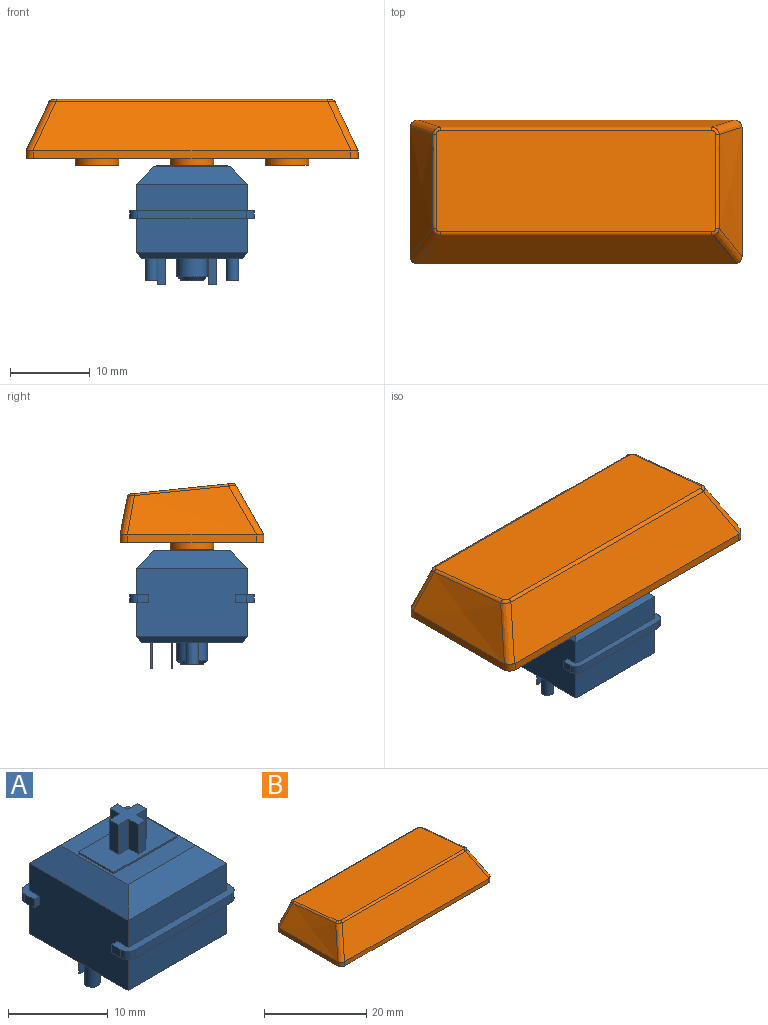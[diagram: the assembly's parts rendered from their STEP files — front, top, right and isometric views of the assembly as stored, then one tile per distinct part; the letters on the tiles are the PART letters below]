
ASSEMBLY  parts=2 mates=1
PART A: 69 faces, bbox 15.6x15.6x18.6 mm
  f0: plane 15.6x2.3mm, normal (0,0,-1), area 14.4mm2, adj f2,f3,f28,f30,f35,f60,f62,f63
  f1: plane 15.6x2.3mm, normal (0,0,-1), area 14.4mm2, adj f28,f30,f33,f34,f36,f59,f61,f64
  f2: plane 1.3x1mm, normal (1,0,0), area 1.3mm2, adj f0,f32,f62,f66
  f3: plane 1.3x1mm, normal (-1,0,0), area 1.3mm2, adj f0,f32,f63,f68
  f4: plane 15.6x2.3mm, normal (0,0,1), area 14.4mm2, adj f28,f30,f31,f33,f34,f36,f61,f64
  f5: plane 14x2.2mm, normal (-0.71,0,0.71), area 36.7mm2, adj f6,f7,f26,f30
  f6: plane 14x2.2mm, normal (0,-0.71,0.71), area 36.7mm2, adj f5,f7,f27,f31
  f7: plane 9.6x9.6mm, normal (0,0,1), area 47.2mm2, adj f5,f6,f8,f9,f10,f11,f26,f27
  f8: plane 5x0.2mm, normal (1,0,0), area 1mm2, adj f7,f9,f11,f12
  f9: plane 9x0.2mm, normal (0,1,0), area 1.8mm2, adj f7,f8,f10,f12
  f10: plane 5x0.2mm, normal (-1,0,0), area 1mm2, adj f7,f9,f11,f12
  f11: plane 9x0.2mm, normal (0,-1,0), area 1.8mm2, adj f7,f8,f10,f12
  f12: plane 9x5mm, normal (0,0,1), area 36.9mm2, adj f8,f9,f10,f11,f13,f14,f15,f16
  f13: plane 3.6x1.35mm, normal (1,0,0), area 4.9mm2, adj f12,f14,f24,f25
  f14: plane 3.6x1.08mm, normal (0,1,0), area 3.9mm2, adj f12,f13,f15,f25
  f15: plane 3.6x1.35mm, normal (-1,0,0), area 4.9mm2, adj f12,f14,f16,f25
  f16: plane 3.6x1.46mm, normal (0,1,0), area 5.3mm2, adj f12,f15,f17,f25
  f17: plane 3.6x1.3mm, normal (-1,0,0), area 4.7mm2, adj f12,f16,f18,f25
  f18: plane 3.6x1.46mm, normal (0,-1,0), area 5.3mm2, adj f12,f17,f19,f25
  f19: plane 3.6x1.35mm, normal (-1,0,0), area 4.9mm2, adj f12,f18,f20,f25
  f20: plane 3.6x1.08mm, normal (0,-1,0), area 3.9mm2, adj f12,f19,f21,f25
  f21: plane 3.6x1.35mm, normal (1,0,0), area 4.9mm2, adj f12,f20,f22,f25
  f22: plane 3.6x1.46mm, normal (0,-1,0), area 5.3mm2, adj f12,f21,f23,f25
  f23: plane 3.6x1.3mm, normal (1,0,0), area 4.7mm2, adj f12,f22,f24,f25
  f24: plane 3.6x1.46mm, normal (0,1,0), area 5.3mm2, adj f12,f13,f23,f25
  f25: plane 4x4mm, normal (0,0,1), area 8.1mm2, adj f13,f14,f15,f16,f17,f18,f19,f20
  f26: plane 14x2.2mm, normal (0,0.71,0.71), area 36.7mm2, adj f5,f7,f27,f29
  f27: plane 14x2.2mm, normal (0.71,0,0.71), area 36.7mm2, adj f6,f7,f26,f28
  f28: plane 14x8.6mm, normal (1,0,0), area 117.4mm2, adj f0,f1,f4,f27,f29,f31,f32,f55
  f29: plane 14x3.3mm, normal (0,1,0), area 46.2mm2, adj f26,f28,f30,f32
  f30: plane 14x8.6mm, normal (-1,0,0), area 117.4mm2, adj f0,f1,f4,f5,f29,f31,f32,f57
  f31: plane 14x3.3mm, normal (0,-1,0), area 46.2mm2, adj f4,f6,f28,f30
  f32: plane 15.6x2.3mm, normal (0,0,1), area 14.4mm2, adj f2,f3,f28,f29,f30,f35,f62,f63
  f33: plane 13.6x1mm, normal (0,-1,0), area 13.6mm2, adj f1,f4,f61,f64
  f34: plane 1.3x1mm, normal (1,0,0), area 1.3mm2, adj f1,f4,f61,f65
  f35: plane 13.6x1mm, normal (0,1,0), area 13.6mm2, adj f0,f32,f62,f63
  f36: plane 1.3x1mm, normal (-1,0,0), area 1.3mm2, adj f1,f4,f64,f67
  f37: plane 2.85x2.85mm, normal (0,0,-1), area 6.4mm2, adj f38
  f38: cone r=1.43mm half-angle=45deg, axis (0,0,1), area 7.4mm2, adj f37,f43
  f39: plane 1x0.2mm, normal (0,0,-1), area 0.2mm2, adj f44,f45,f46,f47
  f40: plane 1x0.2mm, normal (0,0,-1), area 0.2mm2, adj f48,f49,f50,f51
  f41: plane 1.6x1.6mm, normal (0,0,-1), area 2mm2, adj f52
  f42: plane 1.6x1.6mm, normal (0,0,-1), area 2mm2, adj f53
  f43: cylinder r=1.93mm len=3.85mm, axis (0,0,1), area 27.8mm2, adj f38,f54
  f44: plane 3.3x0.2mm, normal (-1,0,0), area 0.7mm2, adj f39,f45,f47,f54
  f45: plane 3.3x1mm, normal (0,1,0), area 3.3mm2, adj f39,f44,f46,f54
  f46: plane 3.3x0.2mm, normal (1,0,0), area 0.7mm2, adj f39,f45,f47,f54
  f47: plane 3.3x1mm, normal (0,-1,0), area 3.3mm2, adj f39,f44,f46,f54
  f48: plane 3.3x0.2mm, normal (-1,0,0), area 0.7mm2, adj f40,f49,f51,f54
  f49: plane 3.3x1mm, normal (0,1,0), area 3.3mm2, adj f40,f48,f50,f54
  f50: plane 3.3x0.2mm, normal (1,0,0), area 0.7mm2, adj f40,f49,f51,f54
  f51: plane 3.3x1mm, normal (0,-1,0), area 3.3mm2, adj f40,f48,f50,f54
  f52: cylinder r=0.8mm len=2.8mm, axis (0,0,1), area 14.1mm2, adj f41,f54
  f53: cylinder r=0.8mm len=2.8mm, axis (0,0,1), area 14.1mm2, adj f42,f54
  f54: plane 12.6x12.6mm, normal (0,0,-1), area 142.7mm2, adj f43,f44,f45,f46,f47,f48,f49,f50
  f55: plane 14x0.7mm, normal (0.71,0,-0.71), area 13.2mm2, adj f28,f54,f56,f58
  f56: plane 14x0.7mm, normal (0,0.71,-0.71), area 13.2mm2, adj f54,f55,f57,f60
  f57: plane 14x0.7mm, normal (-0.71,0,-0.71), area 13.2mm2, adj f30,f54,f56,f58
  f58: plane 14x0.7mm, normal (0,-0.71,-0.71), area 13.2mm2, adj f54,f55,f57,f59
  f59: plane 14x4.3mm, normal (0,-1,0), area 60.2mm2, adj f1,f28,f30,f58
  f60: plane 14x4.3mm, normal (0,1,0), area 60.2mm2, adj f0,f28,f30,f56
  f61: cylinder r=1mm len=1mm, axis (0,0,-1), area 1.6mm2, adj f1,f4,f33,f34
  f62: cylinder r=1mm len=1mm, axis (0,0,1), area 1.6mm2, adj f0,f2,f32,f35
  f63: cylinder r=1mm len=1mm, axis (0,0,-1), area 1.6mm2, adj f0,f3,f32,f35
  f64: cylinder r=1mm len=1mm, axis (0,0,1), area 1.6mm2, adj f1,f4,f33,f36
  f65: plane 1x0.8mm, normal (0,1,0), area 0.8mm2, adj f1,f4,f28,f34
  f66: plane 1x0.8mm, normal (0,-1,0), area 0.8mm2, adj f0,f2,f28,f32
  f67: plane 1x0.8mm, normal (0,1,0), area 0.8mm2, adj f1,f4,f30,f36
  f68: plane 1x0.8mm, normal (0,-1,0), area 0.8mm2, adj f0,f3,f30,f32
PART B: 80 faces, bbox 44.9x21.6x10.6 mm
  f0: plane 41.75x18.1mm, normal (0,0,-1), area 114.8mm2, adj f1,f2,f3,f4,f10,f12,f14,f16
  f1: plane 39.75x1mm, normal (0,-1,0), area 39.8mm2, adj f0,f8,f10,f12
  f2: plane 16.1x1mm, normal (1,0,0), area 16.1mm2, adj f0,f9,f10,f16
  f3: plane 39.75x1mm, normal (0,1,0), area 39.7mm2, adj f0,f6,f14,f15,f16,f17
  f4: plane 16.1x1mm, normal (-1,0,0), area 16.1mm2, adj f0,f7,f12,f14
  f5: plane 35.18x12.74mm, normal (0,0.1,0.99), area 449.7mm2, adj f18,f19,f20,f21,f22,f23,f24,f25
  f6: plane 39.66x4.75mm, normal (0,0.98,0.19), area 178.6mm2, adj f3,f15,f17,f20
  f7: bspline ~18.1x6.51mm, area 88.3mm2, adj f4,f12,f13,f14,f15,f19
  f8: plane 40x6.23mm, normal (0,-0.87,0.49), area 265.5mm2, adj f1,f10,f11,f12,f13,f23
  f9: bspline ~18.1x6.51mm, area 88.3mm2, adj f2,f10,f11,f16,f17,f24
  f10: cylinder r=1mm len=1.08mm, axis (0,0,1), area 1.7mm2, adj f0,f1,f2,f8,f9,f11
  f11: bspline ~8x5.25mm, area 10.6mm2, adj f8,f9,f10,f25
  f12: cylinder r=1mm len=1.08mm, axis (0,0,-1), area 1.7mm2, adj f0,f1,f4,f7,f8,f13
  f13: bspline ~8.02x5.26mm, area 10.6mm2, adj f7,f8,f12,f21
  f14: cylinder r=1mm len=1.01mm, axis (0,0,1), area 1.6mm2, adj f0,f3,f4,f7,f15
  f15: bspline ~7.53x4.96mm, area 8.3mm2, adj f3,f6,f7,f14,f18
  f16: cylinder r=1mm len=1.01mm, axis (0,0,-1), area 1.6mm2, adj f0,f2,f3,f9,f17
  f17: bspline ~7.51x4.95mm, area 8.3mm2, adj f3,f6,f9,f16,f22
  f18: bspline ~1.23x0.97mm, area 0.6mm2, adj f5,f15,f19,f20
  f19: bspline ~17.25x2.02mm, area 6.5mm2, adj f5,f7,f18,f21
  f20: cylinder r=0.5mm len=34.19mm, axis (-1,0,0), area 21.9mm2, adj f5,f6,f18,f22
  f21: bspline ~1.16x0.98mm, area 0.6mm2, adj f5,f13,f19,f23
  f22: bspline ~1.23x1.14mm, area 0.6mm2, adj f5,f17,f20,f24
  f23: cylinder r=0.5mm len=34.18mm, axis (-1,0,0), area 19.8mm2, adj f5,f8,f21,f25
  f24: bspline ~17.24x2.02mm, area 6.5mm2, adj f5,f9,f22,f25
  f25: bspline ~1.16x1mm, area 0.6mm2, adj f5,f11,f23,f24
  f26: plane 39.75x0.74mm, normal (0,1,0), area 29.3mm2, adj f0,f27,f29,f33
  f27: plane 16.13x0.81mm, normal (-1,0,0), area 12.2mm2, adj f0,f26,f28,f33,f34
  f28: plane 39.75x0.91mm, normal (0,-1,0), area 36mm2, adj f0,f27,f29,f31,f32,f34
  f29: plane 16.13x0.81mm, normal (1,0,0), area 12.2mm2, adj f0,f26,f28,f32,f33
  f30: plane 35.75x13.18mm, normal (0,-0.1,-0.99), area 346.3mm2, adj f31,f32,f33,f34,f46,f61,f76
  f31: plane 39.57x4.31mm, normal (0,-0.98,-0.19), area 162.1mm2, adj f28,f30,f32,f34
  f32: offset ~20.1x8.51mm, area 80.9mm2, adj f28,f29,f30,f31,f33
  f33: plane 39.78x5.75mm, normal (0,0.87,-0.49), area 243.8mm2, adj f26,f27,f29,f30,f32,f34
  f34: offset ~20.1x8.51mm, area 80.9mm2, adj f27,f28,f30,f31,f33
  f35: plane 6.82x1.5mm, normal (0,1,0), area 10.2mm2, adj f36,f44,f45,f49
  f36: plane 6.82x1.3mm, normal (1,0,0), area 8.8mm2, adj f35,f37,f45,f49
  f37: plane 6.68x1.5mm, normal (0,-1,0), area 10mm2, adj f36,f38,f45,f49
  f38: plane 6.68x1.35mm, normal (1,0,0), area 8.9mm2, adj f37,f39,f45,f49
  f39: plane 6.54x1mm, normal (0,-1,0), area 6.5mm2, adj f38,f40,f45,f49
  f40: plane 6.68x1.35mm, normal (-1,0,0), area 8.9mm2, adj f39,f41,f45,f49
  f41: plane 6.68x1.5mm, normal (0,-1,0), area 10mm2, adj f40,f42,f45,f49
  f42: plane 6.82x1.3mm, normal (-1,0,0), area 8.8mm2, adj f41,f43,f45,f49
  f43: plane 6.82x1.5mm, normal (0,1,0), area 10.2mm2, adj f42,f45,f47,f49
  f44: plane 6.96x1.35mm, normal (1,0,0), area 9.3mm2, adj f35,f45,f48,f49
  f45: plane 5.5x5.5mm, normal (0,0,-1), area 15.9mm2, adj f35,f36,f37,f38,f39,f40,f41,f42
  f46: cylinder r=2.75mm len=6.47mm, axis (0,0,-1), area 111.7mm2, adj f30,f45
  f47: plane 6.96x1.35mm, normal (-1,0,0), area 9.3mm2, adj f43,f45,f48,f49
  f48: plane 6.96x1mm, normal (0,1,0), area 7mm2, adj f44,f45,f47,f49
  f49: plane 4x4mm, normal (0,-0.1,-0.99), area 7.9mm2, adj f35,f36,f37,f38,f39,f40,f41,f42
  f50: plane 6.82x1.3mm, normal (-1,0,0), area 8.8mm2, adj f51,f59,f60,f64
  f51: plane 6.82x1.5mm, normal (0,1,0), area 10.2mm2, adj f50,f52,f60,f64
  f52: plane 6.96x1.35mm, normal (-1,0,0), area 9.3mm2, adj f51,f53,f60,f64
  f53: plane 6.96x1mm, normal (0,1,0), area 7mm2, adj f52,f54,f60,f64
  f54: plane 6.96x1.35mm, normal (1,0,0), area 9.3mm2, adj f53,f55,f60,f64
  f55: plane 6.82x1.5mm, normal (0,1,0), area 10.2mm2, adj f54,f56,f60,f64
  f56: plane 6.82x1.3mm, normal (1,0,0), area 8.8mm2, adj f55,f57,f60,f64
  f57: plane 6.68x1.5mm, normal (0,-1,0), area 10mm2, adj f56,f58,f60,f64
  f58: plane 6.68x1.35mm, normal (1,0,0), area 8.9mm2, adj f57,f60,f62,f64
  f59: plane 6.68x1.5mm, normal (0,-1,0), area 10mm2, adj f50,f60,f63,f64
  f60: plane 5.5x5.5mm, normal (0,0,-1), area 15.9mm2, adj f50,f51,f52,f53,f54,f55,f56,f57
  f61: cylinder r=2.75mm len=6.47mm, axis (0,0,-1), area 111.7mm2, adj f30,f60
  f62: plane 6.54x1mm, normal (0,-1,0), area 6.5mm2, adj f58,f60,f63,f64
  f63: plane 6.68x1.35mm, normal (-1,0,0), area 8.9mm2, adj f59,f60,f62,f64
  f64: plane 4x4mm, normal (0,-0.1,-0.99), area 7.9mm2, adj f50,f51,f52,f53,f54,f55,f56,f57
  f65: plane 6.82x1.3mm, normal (-1,0,0), area 8.8mm2, adj f66,f74,f75,f79
  f66: plane 6.82x1.5mm, normal (0,1,0), area 10.2mm2, adj f65,f67,f75,f79
  f67: plane 6.96x1.35mm, normal (-1,0,0), area 9.3mm2, adj f66,f68,f75,f79
  f68: plane 6.96x1mm, normal (0,1,0), area 7mm2, adj f67,f69,f75,f79
  f69: plane 6.96x1.35mm, normal (1,0,0), area 9.3mm2, adj f68,f70,f75,f79
  f70: plane 6.82x1.5mm, normal (0,1,0), area 10.2mm2, adj f69,f71,f75,f79
  f71: plane 6.82x1.3mm, normal (1,0,0), area 8.8mm2, adj f70,f72,f75,f79
  f72: plane 6.68x1.5mm, normal (0,-1,0), area 10mm2, adj f71,f73,f75,f79
  f73: plane 6.68x1.35mm, normal (1,0,0), area 8.9mm2, adj f72,f75,f77,f79
  f74: plane 6.68x1.5mm, normal (0,-1,0), area 10mm2, adj f65,f75,f78,f79
  f75: plane 5.5x5.5mm, normal (0,0,-1), area 15.9mm2, adj f65,f66,f67,f68,f69,f70,f71,f72
  f76: cylinder r=2.75mm len=6.47mm, axis (0,0,-1), area 111.7mm2, adj f30,f75
  f77: plane 6.54x1mm, normal (0,-1,0), area 6.5mm2, adj f73,f75,f78,f79
  f78: plane 6.68x1.35mm, normal (-1,0,0), area 8.9mm2, adj f74,f75,f77,f79
  f79: plane 4x4mm, normal (0,-0.1,-0.99), area 7.9mm2, adj f65,f66,f67,f68,f69,f70,f71,f72
PLACE A at identity fixed
PLACE B t=(0,0,11.7)mm
MATE fastened B.f46 <-> A.f38  axis (0,0,-1) through (0,0,11.7)mm
